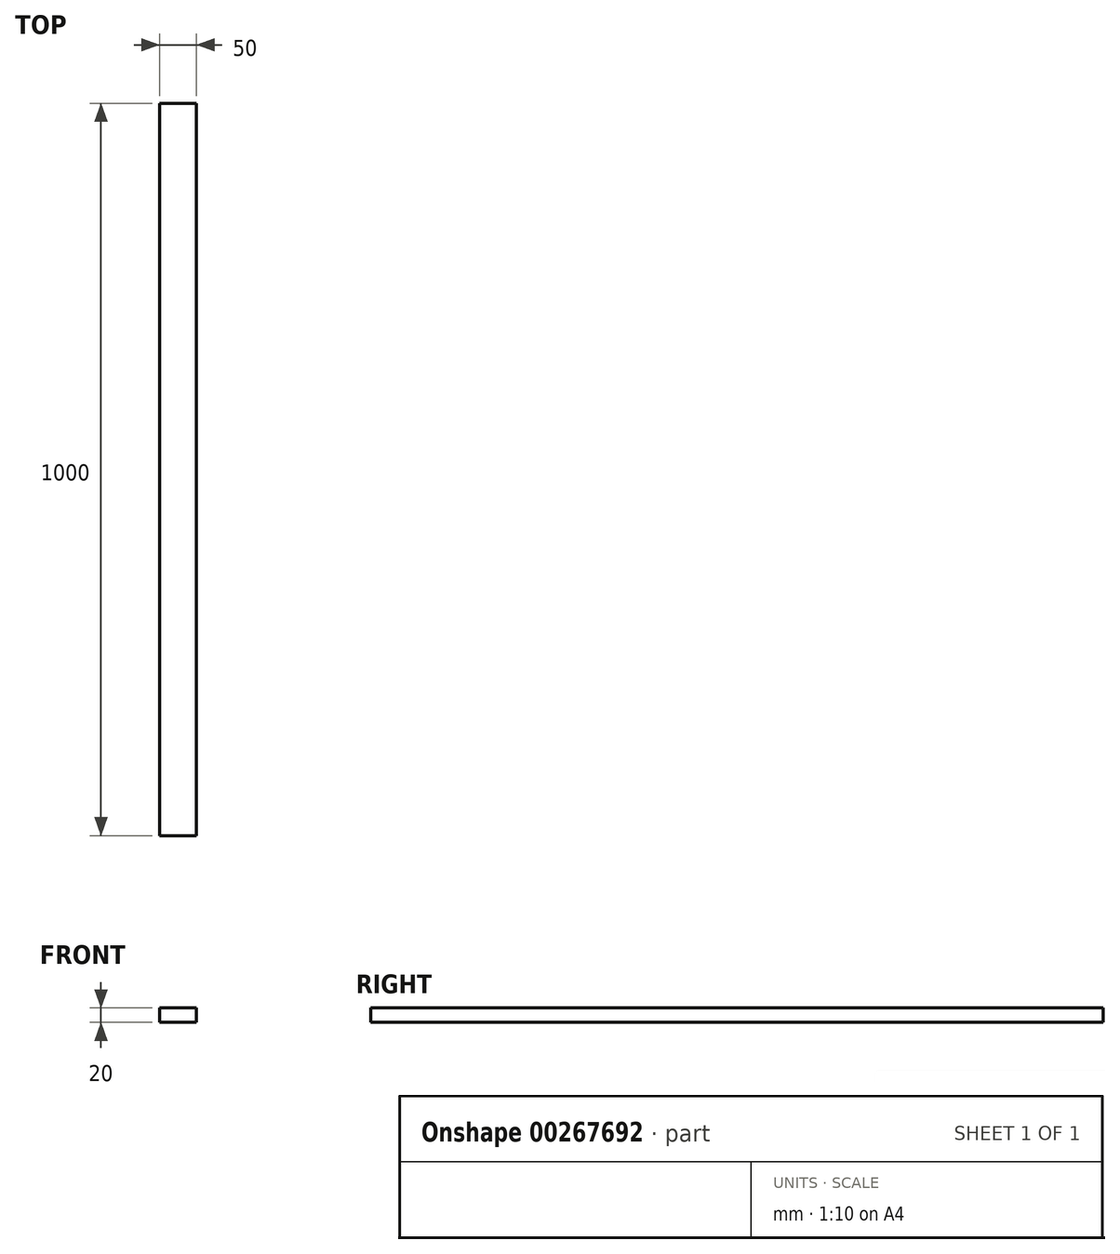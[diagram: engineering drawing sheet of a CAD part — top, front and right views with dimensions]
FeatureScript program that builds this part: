
annotation { "Feature Type Name" : "Feature", "Feature Type Description" : "" }
export const myFeature = defineFeature(function(context is Context, id is Id, definition is map)
    precondition{}
    {
        {
            var Q0;
            Q0=qCreatedBy(makeId("Front.planeOp"),FACE);
            var sketch = newSketch(context, id + "F0", { "sketchPlane" : qUnion([Q0])});
            skLineSegment(sketch, "E0.bottom", {"start": v(25, 10) * mm, "end": v(-25, 10) * mm});
            skLineSegment(sketch, "E0.top", {"start": v(25, -10) * mm, "end": v(-25, -10) * mm});
            skLineSegment(sketch, "E0.left", {"start": v(25, 10) * mm, "end": v(25, -10) * mm});
            skLineSegment(sketch, "E0.right", {"start": v(-25, 10) * mm, "end": v(-25, -10) * mm});
            skPoint(sketch, "E0.middle", {"position": v(0, 0) * mm});
            skSolve(sketch);
        }
        {
            var Q0;
            Q0=makeQuery(id+"F0.imprint","IMPRINT",FACE,{"disambiguationData":[TD([[makeQuery(id+"F0.imprint","IMPRINT",EDGE,{"derivedFrom":sQuery(id+"F0.wireOp",EDGE,"E0.bottom")}),1.0]])]});
            extrude(context, id + "F1", {"entities" : qUnion([Q0]), "oppositeDirection" : true, "depth" : 1000 * mm});
        }
    });
